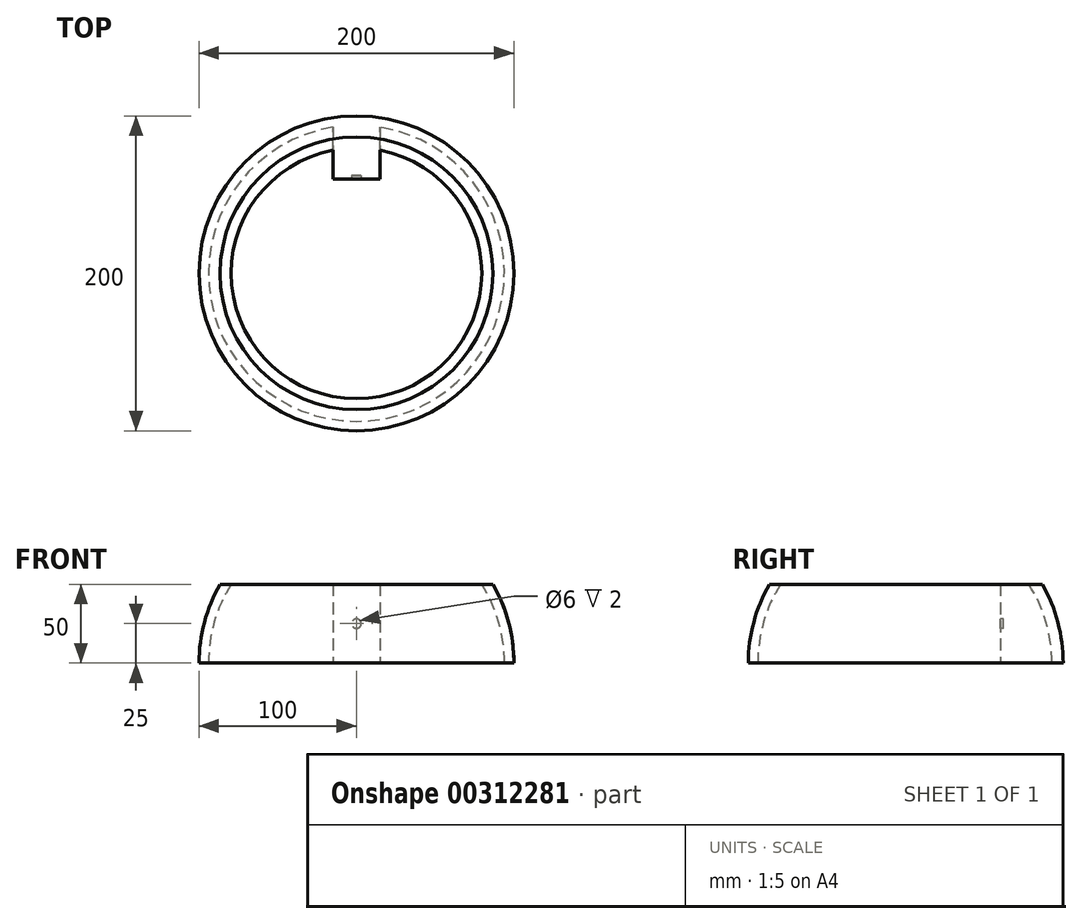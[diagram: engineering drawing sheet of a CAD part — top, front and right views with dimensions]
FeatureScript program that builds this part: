
annotation { "Feature Type Name" : "Feature", "Feature Type Description" : "" }
export const myFeature = defineFeature(function(context is Context, id is Id, definition is map)
    precondition{}
    {
        {
            var Q0;
            Q0=qCreatedBy(makeId("Front.planeOp"),FACE);
            var sketch = newSketch(context, id + "F0", { "sketchPlane" : qUnion([Q0])});
            skArc(sketch, "E0", {"start": v(-86.6, 50) * mm, "mid": v(-96.6, 25.88) * mm, "end": v(-100, 0) * mm});
            skLineSegment(sketch, "E1", {"start": v(0, 50) * mm, "end": v(0, 0) * mm});
            skLineSegment(sketch, "E2", {"start": v(0, 50) * mm, "end": v(-86.6, 50) * mm});
            skLineSegment(sketch, "E3", {"start": v(0, 0) * mm, "end": v(-100, 0) * mm});
            skPoint(sketch, "E4.orphan", {"position": v(0, 100) * mm});
            skSolve(sketch);
        }
        {
            var Q0;
            Q0=qSketchRegion(id+"F0",true);
            var Q1;
            Q1=sQuery(id+"F0.wireOp",EDGE,"E1");
            revolve(context, id + "F1", {"entities" : qUnion([Q0]), "axis" : qUnion([Q1]), "revolveType" : RevolveType.FULL});
        }
        {
            var Q0;
            Q0=makeQuery(id+"F1.opRevolve","SWEPT_FACE",FACE,{"disambiguationData":[OSD([sQuery(id+"F0.wireOp",EDGE,"E2")])]});
            var Q1;
            Q1=makeQuery(id+"F1.opRevolve","SWEPT_FACE",FACE,{"disambiguationData":[OSD([sQuery(id+"F0.wireOp",EDGE,"E3")])]});
            shell(context, id + "F2", {"entities" : qUnion([Q0, Q1]), "thickness" : 6 * mm});
        }
        {
            var Q0;
            Q0=qCreatedBy(makeId("Front.planeOp"),FACE);
            cPlane(context, id + "F3", {"entities" : qUnion([Q0]), "cplaneType" : CPlaneType.OFFSET, "offset" : 60 * mm, "oppositeDirection" : true, "width" : 150 * mm, "height" : 150 * mm});
        }
        {
            var Q0;
            Q0=qCreatedBy(id+"F3.planeOp",FACE);
            var sketch = newSketch(context, id + "F4", { "sketchPlane" : qUnion([Q0])});
            skLineSegment(sketch, "E5.0", {"start": v(-15, 50) * mm, "end": v(15, 50) * mm});
            skLineSegment(sketch, "E6.0", {"start": v(-15, 0) * mm, "end": v(15, 0) * mm});
            skLineSegment(sketch, "E7", {"start": v(15, 50) * mm, "end": v(15, 0) * mm});
            skLineSegment(sketch, "E8", {"start": v(-15, 50) * mm, "end": v(-15, 0) * mm});
            skPoint(sketch, "E9.orphan", {"position": v(-86.6, 50) * mm});
            skPoint(sketch, "E10.orphan", {"position": v(-100, 0) * mm});
            skPoint(sketch, "E11.orphan", {"position": v(86.6, 50) * mm});
            skPoint(sketch, "E12.orphan", {"position": v(100, 0) * mm});
            skSolve(sketch);
        }
        {
            var Q0;
            Q0=qSketchRegion(id+"F4",true);
            extrude(context, id + "F5", {"entities" : qUnion([Q0]), "operationType" : NewBodyOperationType.ADD, "endBound" : BoundingType.UP_TO_NEXT, "oppositeDirection" : true, "depth" : 25 * mm});
        }
        {
            var Q0;
            Q0=makeQuery(id+"F5.opExtrude","CAP_FACE",FACE,{"disambiguationData":[OSD([sQuery(id+"F4.wireOp",EDGE,"E5.0"),sQuery(id+"F4.wireOp",EDGE,"E6.0"),sQuery(id+"F4.wireOp",EDGE,"E7"),sQuery(id+"F4.wireOp",EDGE,"E8")])],"isStart":true});
            var sketch = newSketch(context, id + "F6", { "sketchPlane" : qUnion([Q0])});
            skCircle(sketch, "E13", {"center": v(0, 25) * mm, "radius": 3 * mm});
            skPoint(sketch, "E13.centerSnap0", {"position": v(-15, 25) * mm});
            skSolve(sketch);
        }
        {
            var Q0;
            Q0=qSketchRegion(id+"F6",true);
            extrude(context, id + "F7", {"entities" : qUnion([Q0]), "operationType" : NewBodyOperationType.REMOVE, "oppositeDirection" : true, "depth" : 2 * mm});
        }
    });
